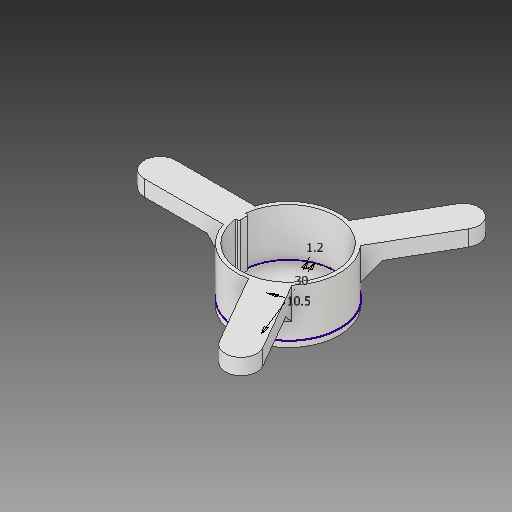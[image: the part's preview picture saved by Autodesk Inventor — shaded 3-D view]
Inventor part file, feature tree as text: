
AUTODESK INVENTOR PART (.ipt)
format: ipt  version: 2018.2 (Build 222227000, 227)  size: 204,288 bytes
history: native  units: mm
features: extrude x7, sketch x5, other x3, plane x1, chamfer x1, pattern_circular x1, projected_geometry x1, reference x1
ambient origin geometry x8: Origin, YZ Plane, XZ Plane, XY Plane, X Axis, Y Axis, Z Axis, Center Point
bodies: Solid1 (feature_tree)
feature tree (20):
  sketch  "Sketch1"  dims[d0=30.0mm d1=1.2mm]
  extrude  "Extrusion1"  Depth=1.2mm
  extrude  "Extrusion2"  Depth=5.0mm
  plane  "Work Plane1"
  sketch  "Sketch2"  dims[d2=5.0mm d3=25.0mm]
  extrude  "Extrusion3"  Depth=2.0mm TaperAngle=0.0deg
  extrude  "Extrusion4"  Depth=10.0mm
  chamfer  "Chamfer1"  Distance=30.0mm
  pattern_circular  "Circular Pattern1"  [2 undecoded]
  extrude  "Extrusion6"  TaperAngle=0.0deg  [1 undecoded]
  extrude  "Extrusion7"  Depth=2.0mm TaperAngle=360.0deg
  extrude  "Extrusion8"  Depth=2.0mm
  sketch  "Sketch4"  dims[d4=5.0mm d5=2.0mm d6=0.0mm]
  projected_geometry  "Projected Loop2"
  sketch  "Sketch5"  dims[d7=2.0mm d8=0.0mm d9=10.0mm]
  reference  "Reference1"
  sketch  "Sketch6"  dims[d10=10.5mm d12=30.0mm d13=2.0mm d14=0.0mm d15=0.0mm d16=0.0mm d17=30.0mm d18=360.0deg d22=1.2mm d23=5.0mm d24=2.0mm d25=45.0deg d26=3.0mm d27=0.0mm d28=2.0mm d29=0.0mm d30=3.0mm d32=1.0mm d33=0.5mm d34=2.0mm d35=0.0mm]
  other  "<userpath>\OneDrive\Documents\2018 UBC\ELEC 391\Controller\CAD\Pok Mk3.iam"
  other  "Pok Mk3.iam"
  other  "Pok Mk3 Yaw Motor Support:4"
note: 3 required parameter values undecoded (feature->parameter linkage not recoverable at this tier; creation-order binding heuristic only, values carry confidence <= 0.55)
